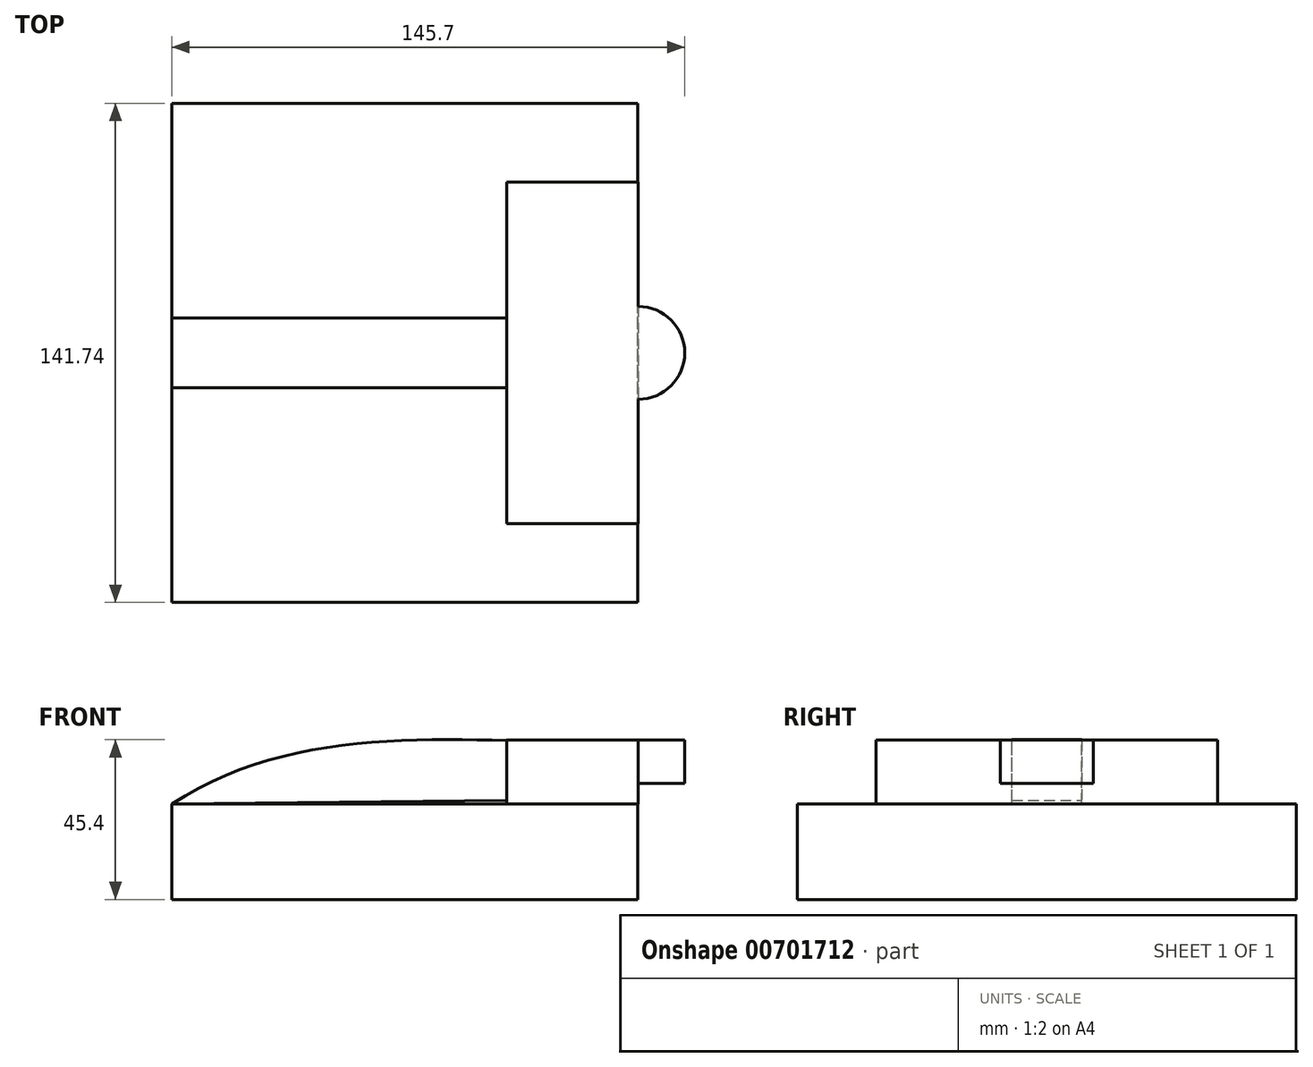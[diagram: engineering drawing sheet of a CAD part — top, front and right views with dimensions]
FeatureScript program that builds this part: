
annotation { "Feature Type Name" : "Feature", "Feature Type Description" : "" }
export const myFeature = defineFeature(function(context is Context, id is Id, definition is map)
    precondition{}
    {
        {
            var Q0;
            Q0=qCreatedBy(makeId("Front.planeOp"),FACE);
            var sketch = newSketch(context, id + "F0", { "sketchPlane" : qUnion([Q0])});
            skLineSegment(sketch, "E0", {"start": v(-59.6, -18.86) * mm, "end": v(-59.6, -44.3) * mm});
            skLineSegment(sketch, "E1", {"start": v(-59.6, -44.3) * mm, "end": v(-34.16, -44.3) * mm});
            skLineSegment(sketch, "E2", {"start": v(-34.16, -44.3) * mm, "end": v(-34.16, -18.86) * mm});
            skLineSegment(sketch, "E3", {"start": v(-34.16, -18.86) * mm, "end": v(-59.6, -18.86) * mm});
            skSolve(sketch);
        }
        {
            var Q0;
            Q0=makeQuery(id+"F0.imprint","IMPRINT",FACE,{"disambiguationData":[TD([[makeQuery(id+"F0.imprint","IMPRINT",EDGE,{"derivedFrom":sQuery(id+"F0.wireOp",EDGE,"E0")}),1.0]])]});
            extrude(context, id + "F1", {"entities" : qUnion([Q0]), "depth" : 41.66 * mm, "offsetDistance" : 25.4 * mm});
        }
        {
            var Q0;
            Q0=qCreatedBy(makeId("Front.planeOp"),FACE);
            var sketch = newSketch(context, id + "F2", { "sketchPlane" : qUnion([Q0])});
            skLineSegment(sketch, "E4", {"start": v(-43.18, 53.44) * mm, "end": v(-15.49, 53.44) * mm});
            skLineSegment(sketch, "E5", {"start": v(-15.49, 53.44) * mm, "end": v(-15.49, 32.72) * mm});
            skLineSegment(sketch, "E6", {"start": v(-43.18, 53.44) * mm, "end": v(-43.18, 32.72) * mm});
            skLineSegment(sketch, "E7", {"start": v(-43.18, 32.72) * mm, "end": v(-15.49, 32.72) * mm});
            skSolve(sketch);
        }
        {
            var Q0;
            Q0=makeQuery(id+"F2.imprint","IMPRINT",FACE,{"disambiguationData":[TD([[makeQuery(id+"F2.imprint","IMPRINT",EDGE,{"derivedFrom":sQuery(id+"F2.wireOp",EDGE,"E4")}),-1.0]])]});
            extrude(context, id + "F3", {"entities" : qUnion([Q0]), "depth" : 25.4 * mm, "offsetDistance" : 25.4 * mm});
        }
        {
            var Q0;
            Q0=qCreatedBy(makeId("Front.planeOp"),FACE);
            var sketch = newSketch(context, id + "F4", { "sketchPlane" : qUnion([Q0])});
            skLineSegment(sketch, "E8", {"start": v(11.18, 9.95) * mm, "end": v(62.06, 9.95) * mm});
            skLineSegment(sketch, "E9", {"start": v(62.06, 9.95) * mm, "end": v(34.57, 55.7) * mm});
            skLineSegment(sketch, "E10", {"start": v(34.57, 55.7) * mm, "end": v(11.18, 9.95) * mm});
            skSolve(sketch);
        }
        {
            var Q0;
            Q0=makeQuery(id+"F4.imprint","IMPRINT",FACE,{"disambiguationData":[TD([[makeQuery(id+"F4.imprint","IMPRINT",EDGE,{"derivedFrom":sQuery(id+"F4.wireOp",EDGE,"E8")}),1.0]])]});
            extrude(context, id + "F5", {"entities" : qUnion([Q0]), "depth" : 25.4 * mm, "offsetDistance" : 25.4 * mm});
        }
        {
            var Q0;
            Q0=makeQuery(id+"F1.opExtrude","SWEPT_BODY",BODY,{"disambiguationData":[OSD([sQuery(id+"F0.wireOp",EDGE,"E0"),sQuery(id+"F0.wireOp",EDGE,"E1"),sQuery(id+"F0.wireOp",EDGE,"E2"),sQuery(id+"F0.wireOp",EDGE,"E3")])]});
            var Q1;
            Q1=makeQuery(id+"F3.opExtrude","SWEPT_BODY",BODY,{"disambiguationData":[OSD([sQuery(id+"F2.wireOp",EDGE,"E4"),sQuery(id+"F2.wireOp",EDGE,"E5"),sQuery(id+"F2.wireOp",EDGE,"E6"),sQuery(id+"F2.wireOp",EDGE,"E7")])]});
            var Q2;
            Q2=makeQuery(id+"F5.opExtrude","SWEPT_BODY",BODY,{"disambiguationData":[OSD([sQuery(id+"F4.wireOp",EDGE,"E8"),sQuery(id+"F4.wireOp",EDGE,"E9"),sQuery(id+"F4.wireOp",EDGE,"E10")])]});
            deleteBodies(context, id + "F6", {"entities" : qUnion([Q0, Q1, Q2])});
        }
        {
            var Q0;
            Q0=qCreatedBy(makeId("Front.planeOp"),FACE);
            var sketch = newSketch(context, id + "F7", { "sketchPlane" : qUnion([Q0])});
            skLineSegment(sketch, "E11.bottom", {"start": v(-62.82, 11.72) * mm, "end": v(69.5, 11.72) * mm});
            skLineSegment(sketch, "E11.top", {"start": v(-62.82, -15.36) * mm, "end": v(69.5, -15.36) * mm});
            skLineSegment(sketch, "E11.left", {"start": v(-62.82, 11.72) * mm, "end": v(-62.82, -15.36) * mm});
            skLineSegment(sketch, "E11.right", {"start": v(69.5, 11.72) * mm, "end": v(69.5, -15.36) * mm});
            skSolve(sketch);
        }
        {
            var Q0;
            Q0=qCreatedBy(makeId("Front.planeOp"),FACE);
            var sketch = newSketch(context, id + "F8", { "sketchPlane" : qUnion([Q0])});
            skLineSegment(sketch, "E12.bottom", {"start": v(32.38, 29.97) * mm, "end": v(69.71, 29.97) * mm});
            skLineSegment(sketch, "E12.top", {"start": v(32.38, 11.72) * mm, "end": v(69.71, 11.72) * mm});
            skLineSegment(sketch, "E12.left", {"start": v(32.38, 29.97) * mm, "end": v(32.38, 11.72) * mm});
            skLineSegment(sketch, "E12.right", {"start": v(69.71, 29.97) * mm, "end": v(69.71, 11.72) * mm});
            skSolve(sketch);
        }
        {
            var Q0;
            Q0=qCreatedBy(makeId("Front.planeOp"),FACE);
            var sketch = newSketch(context, id + "F9", { "sketchPlane" : qUnion([Q0])});
            skLineSegment(sketch, "E13.bottom", {"start": v(69.71, 29.97) * mm, "end": v(82.88, 29.97) * mm});
            skLineSegment(sketch, "E13.top", {"start": v(69.71, 17.61) * mm, "end": v(82.88, 17.61) * mm});
            skLineSegment(sketch, "E13.left", {"start": v(69.71, 29.97) * mm, "end": v(69.71, 17.61) * mm});
            skLineSegment(sketch, "E13.right", {"start": v(82.88, 29.97) * mm, "end": v(82.88, 17.61) * mm});
            skSolve(sketch);
        }
        {
            var Q0;
            Q0=qCreatedBy(makeId("Front.planeOp"),FACE);
            var sketch = newSketch(context, id + "F10", { "sketchPlane" : qUnion([Q0])});
            skFitSpline(sketch, "E14", {"points": [v(-62.82, 11.76) * mm, v(32.38, 29.82) * mm], "startDerivative": vector(85.9, 56.17) * mm, "endDerivative": vector(97.15, -2.23) * mm});
            skLineSegment(sketch, "E15", {"start": v(-62.82, 11.76) * mm, "end": v(32.38, 12.82) * mm});
            skLineSegment(sketch, "E16", {"start": v(32.38, 12.82) * mm, "end": v(32.38, 29.82) * mm});
            skSolve(sketch);
        }
        {
            var Q0;
            Q0=makeQuery(id+"F7.imprint","IMPRINT",FACE,{"disambiguationData":[TD([[makeQuery(id+"F7.imprint","IMPRINT",EDGE,{"derivedFrom":sQuery(id+"F7.wireOp",EDGE,"E11.bottom")}),-1.0]])]});
            extrude(context, id + "F11", {"entities" : qUnion([Q0]), "endBound" : BoundingType.SYMMETRIC, "depth" : 141.73 * mm, "offsetDistance" : 25.4 * mm});
        }
        {
            var Q0;
            Q0=makeQuery(id+"F8.imprint","IMPRINT",FACE,{"disambiguationData":[TD([[makeQuery(id+"F8.imprint","IMPRINT",EDGE,{"derivedFrom":sQuery(id+"F8.wireOp",EDGE,"E12.bottom")}),-1.0]])]});
            extrude(context, id + "F12", {"entities" : qUnion([Q0]), "operationType" : NewBodyOperationType.ADD, "endBound" : BoundingType.SYMMETRIC, "depth" : 97.03 * mm, "offsetDistance" : 25.4 * mm});
        }
        {
            var Q0;
            Q0 = qSketchRegion(id + "F10", true);
            extrude(context, id + "F13", {"entities" : qUnion([Q0]), "operationType" : NewBodyOperationType.ADD, "endBound" : BoundingType.SYMMETRIC, "depth" : 19.8 * mm, "offsetDistance" : 25.4 * mm});
        }
        {
            var Q0;
            Q0=makeQuery(id+"F9.imprint","IMPRINT",FACE,{"disambiguationData":[TD([[makeQuery(id+"F9.imprint","IMPRINT",EDGE,{"derivedFrom":sQuery(id+"F9.wireOp",EDGE,"E13.bottom")}),-1.0]])]});
            var Q1;
            Q1=sQuery(id+"F9.wireOp",EDGE,"E13.left");
            revolve(context, id + "F14", {"operationType" : NewBodyOperationType.ADD, "entities" : qUnion([Q0]), "axis" : qUnion([Q1]), "revolveType" : RevolveType.FULL});
        }
    });
